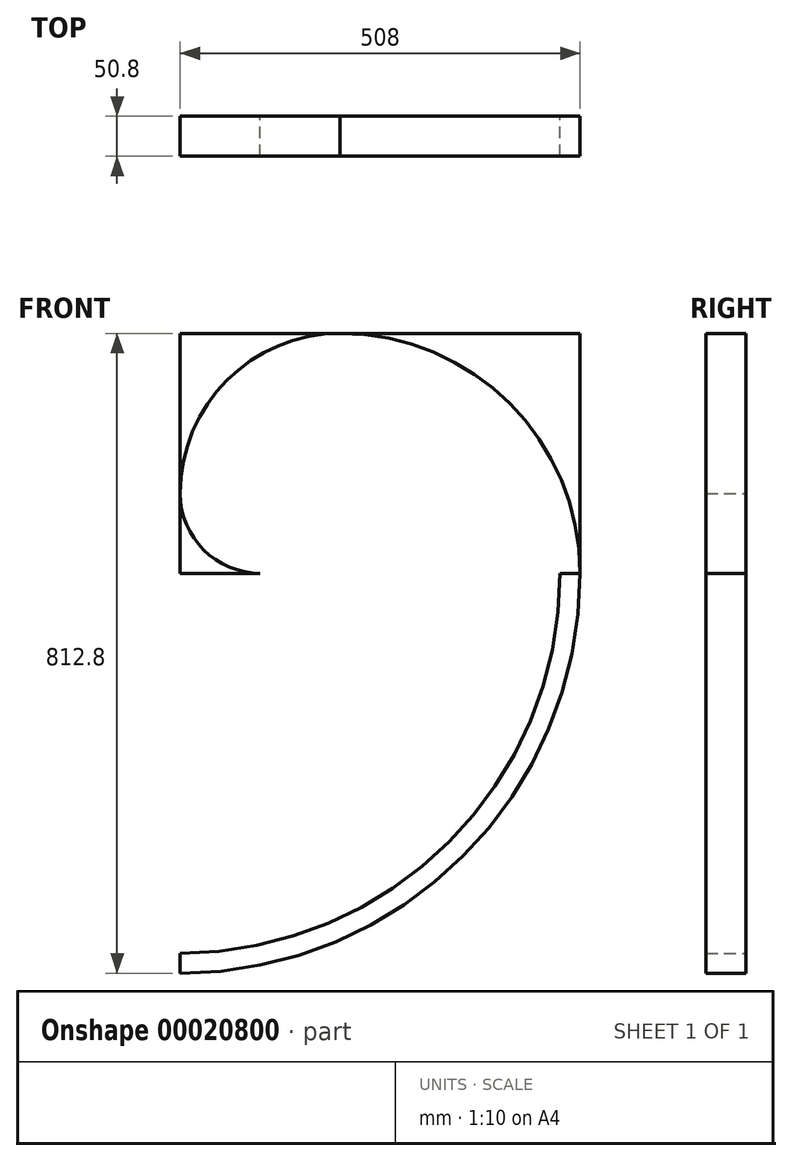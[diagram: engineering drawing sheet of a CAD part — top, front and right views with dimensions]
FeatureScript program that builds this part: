
annotation { "Feature Type Name" : "Feature", "Feature Type Description" : "" }
export const myFeature = defineFeature(function(context is Context, id is Id, definition is map)
    precondition{}
    {
        {
            var Q0;
            Q0=qCreatedBy(makeId("Front.planeOp"),FACE);
            var sketch = newSketch(context, id + "F0", { "sketchPlane" : qUnion([Q0])});
            skLineSegment(sketch, "E0.rect.bottom", {"start": v(50.8, -50.8) * mm, "end": v(-50.8, -50.8) * mm});
            skLineSegment(sketch, "E0.rect.top", {"start": v(50.8, 50.8) * mm, "end": v(-50.8, 50.8) * mm});
            skLineSegment(sketch, "E0.rect.left", {"start": v(50.8, -50.8) * mm, "end": v(50.8, 50.8) * mm});
            skLineSegment(sketch, "E0.rect.right", {"start": v(-50.8, -50.8) * mm, "end": v(-50.8, 50.8) * mm});
            skPoint(sketch, "E0.rect.middle", {"position": v(0, 0) * mm});
            skLineSegment(sketch, "E1.rect.bottom", {"start": v(50.8, -50.8) * mm, "end": v(152.4, -50.8) * mm});
            skLineSegment(sketch, "E1.rect.top", {"start": v(50.8, 50.8) * mm, "end": v(152.4, 50.8) * mm});
            skLineSegment(sketch, "E1.rect.right", {"start": v(152.4, -50.8) * mm, "end": v(152.4, 50.8) * mm});
            skPoint(sketch, "E1.rect.middle", {"position": v(101.6, 0) * mm});
            skLineSegment(sketch, "E2.rect.bottom", {"start": v(152.4, 50.8) * mm, "end": v(-50.8, 50.8) * mm});
            skLineSegment(sketch, "E2.rect.top", {"start": v(152.4, 254) * mm, "end": v(-50.8, 254) * mm});
            skLineSegment(sketch, "E2.rect.left", {"start": v(152.4, 50.8) * mm, "end": v(152.4, 254) * mm});
            skLineSegment(sketch, "E2.rect.right", {"start": v(-50.8, 50.8) * mm, "end": v(-50.8, 254) * mm});
            skPoint(sketch, "E2.rect.middle", {"position": v(50.8, 152.4) * mm});
            skLineSegment(sketch, "E3.bottom", {"start": v(152.4, 254) * mm, "end": v(457.2, 254) * mm});
            skLineSegment(sketch, "E3.top", {"start": v(152.4, -50.8) * mm, "end": v(457.2, -50.8) * mm});
            skLineSegment(sketch, "E3.left", {"start": v(152.4, 254) * mm, "end": v(152.4, -50.8) * mm});
            skLineSegment(sketch, "E3.right", {"start": v(457.2, 254) * mm, "end": v(457.2, -50.8) * mm});
            skLineSegment(sketch, "E4.bottom", {"start": v(-50.8, -50.8) * mm, "end": v(457.2, -50.8) * mm});
            skLineSegment(sketch, "E4.top", {"start": v(-50.8, -558.8) * mm, "end": v(457.2, -558.8) * mm});
            skLineSegment(sketch, "E4.left", {"start": v(-50.8, -50.8) * mm, "end": v(-50.8, -558.8) * mm});
            skLineSegment(sketch, "E4.right", {"start": v(457.2, -50.8) * mm, "end": v(457.2, -558.8) * mm});
            skArc(sketch, "E5", {"start": v(50.8, -50.8) * mm, "mid": v(-21.04, -21.04) * mm, "end": v(-50.8, 50.8) * mm});
            skArc(sketch, "E6", {"start": v(-50.8, 50.8) * mm, "mid": v(8.72, 194.48) * mm, "end": v(152.4, 254) * mm});
            skArc(sketch, "E7", {"start": v(152.4, 254) * mm, "mid": v(367.93, 164.73) * mm, "end": v(457.2, -50.8) * mm});
            skArc(sketch, "E8", {"start": v(-50.8, -558.8) * mm, "mid": v(308.41, -410.01) * mm, "end": v(457.2, -50.8) * mm});
            skArc(sketch, "E9.0", {"start": v(-50.8, -533.4) * mm, "mid": v(290.45, -392.05) * mm, "end": v(431.8, -50.8) * mm});
            skArc(sketch, "E9.1", {"start": v(152.4, 228.6) * mm, "mid": v(349.97, 146.77) * mm, "end": v(431.8, -50.8) * mm});
            skArc(sketch, "E9.2", {"start": v(-25.4, 50.8) * mm, "mid": v(26.68, 176.52) * mm, "end": v(152.4, 228.6) * mm});
            skArc(sketch, "E9.3", {"start": v(50.8, -25.4) * mm, "mid": v(-3.08, -3.08) * mm, "end": v(-25.4, 50.8) * mm});
            skLineSegment(sketch, "E10", {"start": v(-50.8, -242.84) * mm, "end": v(152.4, -50.8) * mm});
            skSolve(sketch);
        }
        {
            var Q0;
            {var subQ0=sQuery(id+"F0.wireOp",EDGE,"E6");Q0=makeQuery(id+"F0.imprint","IMPRINT",FACE,{"disambiguationData":[TD([[makeQuery(id+"F0.imprint","IMPRINT",EDGE,{"derivedFrom":subQ0}),-1.0]])]});}
            var Q1;
            {var subQ0=sQuery(id+"F0.wireOp",EDGE,"E5");Q1=makeQuery(id+"F0.imprint","IMPRINT",FACE,{"disambiguationData":[TD([[makeQuery(id+"F0.imprint","IMPRINT",EDGE,{"derivedFrom":subQ0}),-1.0]])]});}
            var Q2;
            {var subQ0=sQuery(id+"F0.wireOp",EDGE,"E7");Q2=makeQuery(id+"F0.imprint","IMPRINT",FACE,{"disambiguationData":[TD([[makeQuery(id+"F0.imprint","IMPRINT",EDGE,{"derivedFrom":subQ0}),-1.0]])]});}
            var Q3;
            {var subQ0=sQuery(id+"F0.wireOp",EDGE,"E8");Q3=makeQuery(id+"F0.imprint","IMPRINT",FACE,{"disambiguationData":[TD([[makeQuery(id+"F0.imprint","IMPRINT",EDGE,{"derivedFrom":subQ0}),1.0]])]});}
            extrude(context, id + "F1", {"entities" : qUnion([Q0, Q1, Q2, Q3]), "depth" : 50.8 * mm});
        }
    });
